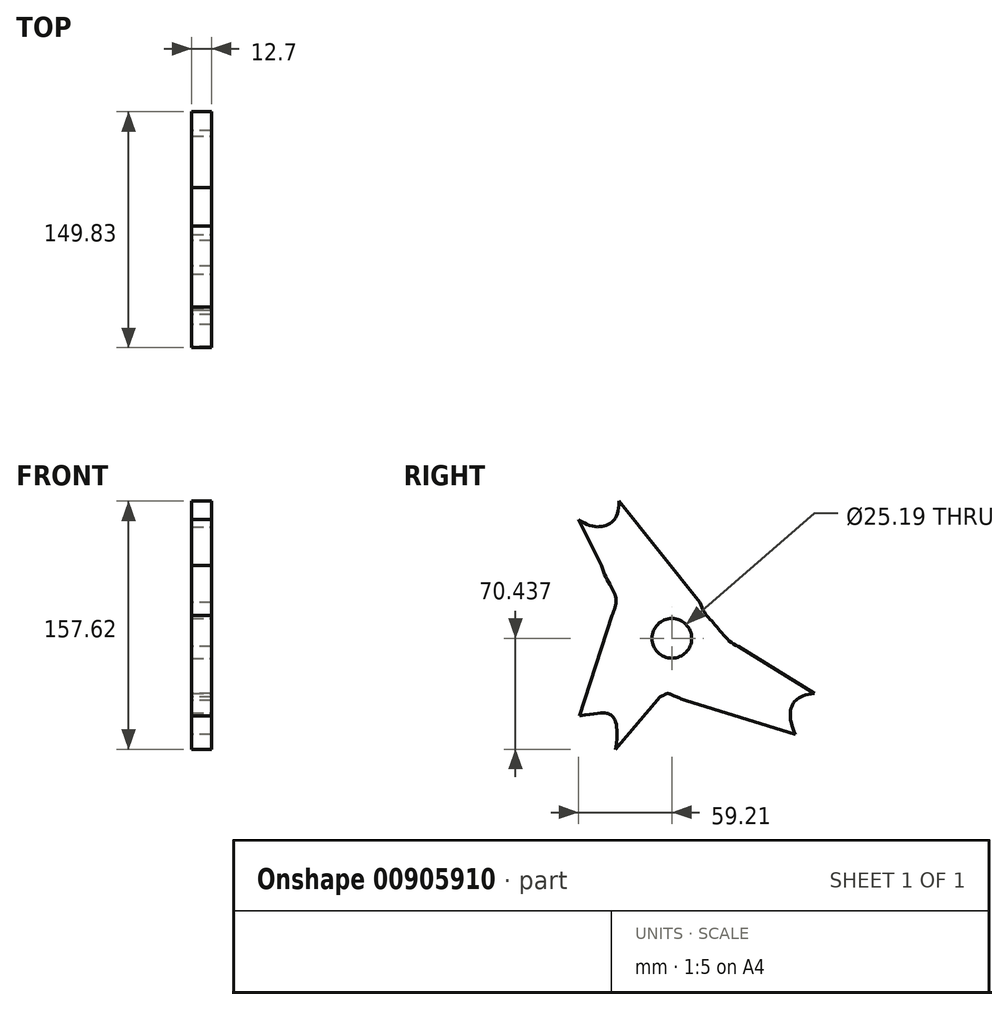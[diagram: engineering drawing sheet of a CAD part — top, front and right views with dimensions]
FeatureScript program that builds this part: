
annotation { "Feature Type Name" : "Feature", "Feature Type Description" : "" }
export const myFeature = defineFeature(function(context is Context, id is Id, definition is map)
    precondition{}
    {
        {
            var Q0;
            Q0=qCreatedBy(makeId("Right.planeOp"),FACE);
            var sketch = newSketch(context, id + "F0", { "sketchPlane" : qUnion([Q0])});
            skFitSpline(sketch, "E0", {"points": [v(-57.38, 60.98) * mm, v(-38.84, 57.75) * mm, v(-31.68, 72.66) * mm], "startDerivative": vector(41.63, -32.34) * mm, "endDerivative": vector(1.08, 56.29) * mm});
            skLineSegment(sketch, "E1", {"start": v(-31.68, 72.66) * mm, "end": v(19.78, 8.45) * mm});
            skFitSpline(sketch, "E2", {"points": [v(19.78, 8.45) * mm, v(29.43, -6.03) * mm, v(44.15, -19.6) * mm], "startDerivative": vector(10.66, -41.67) * mm, "endDerivative": vector(38.25, -14.26) * mm});
            skLineSegment(sketch, "E3", {"start": v(44.15, -19.6) * mm, "end": v(92.45, -49.54) * mm});
            skFitSpline(sketch, "E4", {"points": [v(92.45, -49.54) * mm, v(78.56, -56.64) * mm, v(80.42, -75.46) * mm], "startDerivative": vector(-50.02, -5.4) * mm, "endDerivative": vector(23.25, -45.12) * mm});
            skLineSegment(sketch, "E5", {"start": v(80.42, -75.46) * mm, "end": v(10.64, -54.03) * mm});
            skFitSpline(sketch, "E6", {"points": [v(10.64, -54.03) * mm, v(0, -49.63) * mm, v(-5.7, -51.8) * mm], "startDerivative": vector(-22.07, 8.13) * mm, "endDerivative": vector(-33.77, -16) * mm});
            skLineSegment(sketch, "E7", {"start": v(-5.7, -51.8) * mm, "end": v(-33.92, -84.96) * mm});
            skFitSpline(sketch, "E8", {"points": [v(-33.92, -84.96) * mm, v(-36.69, -63.3) * mm, v(-56.82, -63.7) * mm], "startDerivative": vector(13.12, 87.52) * mm, "endDerivative": vector(-87, -12.89) * mm});
            skLineSegment(sketch, "E9", {"start": v(-56.82, -63.7) * mm, "end": v(-36.27, 0) * mm});
            skFitSpline(sketch, "E10", {"points": [v(-36.27, 0) * mm, v(-33.97, 12.04) * mm, v(-42.84, 31.91) * mm], "startDerivative": vector(14.25, 32.18) * mm, "endDerivative": vector(-13.12, 48.6) * mm});
            skLineSegment(sketch, "E11", {"start": v(-42.84, 31.91) * mm, "end": v(-57.38, 60.98) * mm});
            skSolve(sketch);
        }
        {
            var Q0;
            Q0 = qSketchRegion(id + "F0", true);
            extrude(context, id + "F1", {"entities" : qUnion([Q0]), "depth" : 12.7 * mm, "offsetDistance" : 25.4 * mm});
        }
        {
            var Q0;
            Q0=makeQuery(id+"F1.opExtrude","CAP_FACE",FACE,{"disambiguationData":[OSD([sQuery(id+"F0.wireOp",EDGE,"E0"),sQuery(id+"F0.wireOp",EDGE,"E1"),sQuery(id+"F0.wireOp",EDGE,"E2"),sQuery(id+"F0.wireOp",EDGE,"E3"),sQuery(id+"F0.wireOp",EDGE,"E4"),sQuery(id+"F0.wireOp",EDGE,"E5"),sQuery(id+"F0.wireOp",EDGE,"E6"),sQuery(id+"F0.wireOp",EDGE,"E7"),sQuery(id+"F0.wireOp",EDGE,"E8"),sQuery(id+"F0.wireOp",EDGE,"E9"),sQuery(id+"F0.wireOp",EDGE,"E10"),sQuery(id+"F0.wireOp",EDGE,"E11")])],"isStart":false});
            var sketch = newSketch(context, id + "F2", { "sketchPlane" : qUnion([Q0])});
            skCircle(sketch, "E12", {"center": v(1.83, -14.52) * mm, "radius": 12.6 * mm});
            skSolve(sketch);
        }
        {
            var Q0;
            Q0 = qSketchRegion(id + "F2", true);
            extrude(context, id + "F3", {"entities" : qUnion([Q0]), "operationType" : NewBodyOperationType.REMOVE, "oppositeDirection" : true, "depth" : 12.7 * mm, "offsetDistance" : 25.4 * mm});
        }
    });
